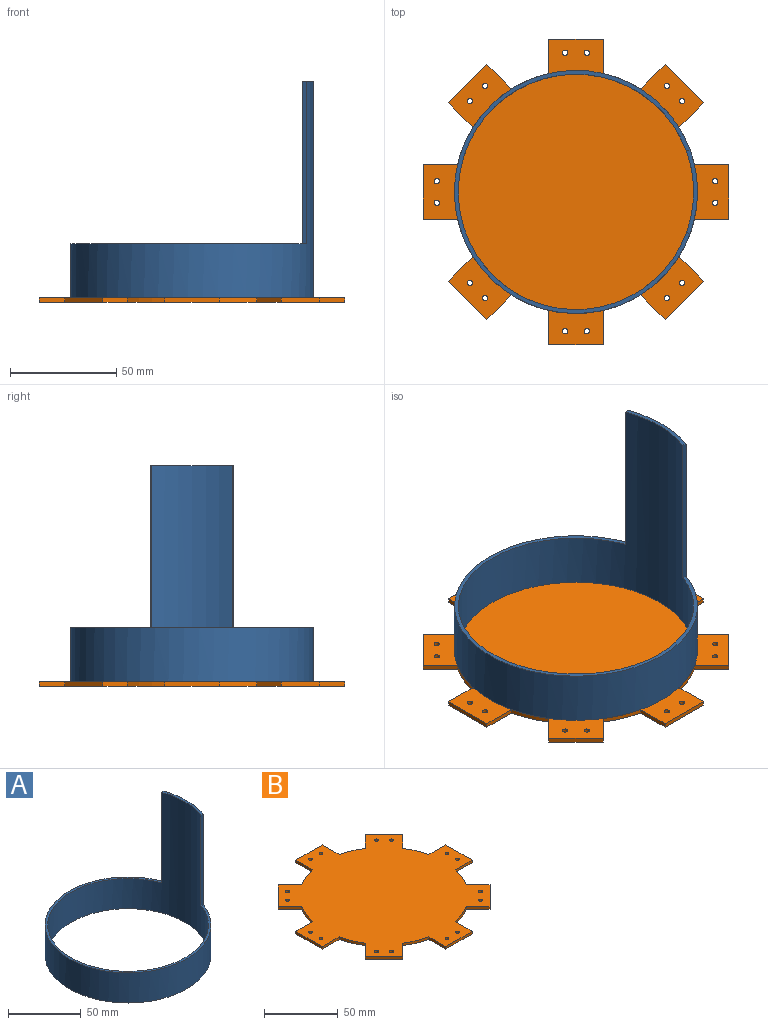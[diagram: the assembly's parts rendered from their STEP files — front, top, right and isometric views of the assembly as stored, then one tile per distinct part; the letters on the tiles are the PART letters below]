
ASSEMBLY  parts=2 mates=1
PART A: 7 faces, bbox 114.3x114.3x101.6 mm
  f0: plane 114.3x110.8mm, normal (0,0,1), area 573.9mm2, adj f1,f2,f4,f5
  f1: cylinder r=55.32mm len=110.64mm, axis (0,0,-1), area 11792.8mm2, adj f0,f3,f4,f5,f6
  f2: cylinder r=57.15mm len=114.3mm, axis (0,0,-1), area 12182.6mm2, adj f0,f3,f4,f5,f6
  f3: plane 114.3x114.3mm, normal (0,0,-1), area 646.2mm2, adj f1,f2
  f4: plane 76.2x1.72mm, normal (-0.34,0.94,0), area 139.4mm2, adj f0,f1,f2,f6
  f5: plane 76.2x1.72mm, normal (-0.34,-0.94,0), area 139.4mm2, adj f0,f1,f2,f6
  f6: plane 39.36x5.21mm, normal (0,0,1), area 72.3mm2, adj f1,f2,f4,f5
PART B: 50 faces, bbox 143.8x143.8x2 mm
  f0: cylinder r=57.15mm len=17.72mm, axis (0,0,-1), area 39.2mm2, adj f1,f31,f32,f33
  f1: plane 11.45x11.45mm, normal (-0.71,-0.71,0), area 32.9mm2, adj f0,f2,f32,f33
  f2: plane 17.96x17.96mm, normal (0.71,-0.71,0), area 51.6mm2, adj f1,f3,f32,f33
  f3: plane 11.45x11.45mm, normal (0.71,0.71,0), area 32.9mm2, adj f2,f4,f32,f33
  f4: cylinder r=57.15mm len=17.72mm, axis (0,0,-1), area 39.2mm2, adj f3,f5,f32,f33
  f5: plane 16.19x2.03mm, normal (0,-1,0), area 32.9mm2, adj f4,f6,f32,f33
  f6: plane 25.4x2.03mm, normal (1,0,0), area 51.6mm2, adj f5,f7,f32,f33
  f7: plane 16.19x2.03mm, normal (0,1,0), area 32.9mm2, adj f6,f8,f32,f33
  f8: cylinder r=57.15mm len=17.72mm, axis (0,0,-1), area 39.2mm2, adj f7,f9,f32,f33
  f9: plane 11.45x11.45mm, normal (0.71,-0.71,0), area 32.9mm2, adj f8,f10,f32,f33
  f10: plane 17.96x17.96mm, normal (0.71,0.71,0), area 51.6mm2, adj f9,f11,f32,f33
  f11: plane 11.45x11.45mm, normal (-0.71,0.71,0), area 32.9mm2, adj f10,f12,f32,f33
  f12: cylinder r=57.15mm len=17.72mm, axis (0,0,-1), area 39.2mm2, adj f11,f13,f32,f33
  f13: plane 16.19x2.03mm, normal (1,0,0), area 32.9mm2, adj f12,f14,f32,f33
  f14: plane 25.4x2.03mm, normal (0,1,0), area 51.6mm2, adj f13,f15,f32,f33
  f15: plane 16.19x2.03mm, normal (-1,0,0), area 32.9mm2, adj f14,f16,f32,f33
  f16: cylinder r=57.15mm len=17.72mm, axis (0,0,-1), area 39.2mm2, adj f15,f17,f32,f33
  f17: plane 11.45x11.45mm, normal (0.71,0.71,0), area 32.9mm2, adj f16,f18,f32,f33
  f18: plane 17.96x17.96mm, normal (-0.71,0.71,0), area 51.6mm2, adj f17,f19,f32,f33
  f19: plane 11.45x11.45mm, normal (-0.71,-0.71,0), area 32.9mm2, adj f18,f20,f32,f33
  f20: cylinder r=57.15mm len=17.72mm, axis (0,0,-1), area 39.2mm2, adj f19,f21,f32,f33
  f21: plane 16.19x2.03mm, normal (0,1,0), area 32.9mm2, adj f20,f22,f32,f33
  f22: plane 25.4x2.03mm, normal (-1,0,0), area 51.6mm2, adj f21,f23,f32,f33
  f23: plane 16.19x2.03mm, normal (0,-1,0), area 32.9mm2, adj f22,f24,f32,f33
  f24: cylinder r=57.15mm len=17.72mm, axis (0,0,-1), area 39.2mm2, adj f23,f25,f32,f33
  f25: plane 11.45x11.45mm, normal (-0.71,0.71,0), area 32.9mm2, adj f24,f26,f32,f33
  f26: plane 17.96x17.96mm, normal (-0.71,-0.71,0), area 51.6mm2, adj f25,f27,f32,f33
  f27: plane 11.45x11.45mm, normal (0.71,-0.71,0), area 32.9mm2, adj f26,f28,f32,f33
  f28: cylinder r=57.15mm len=17.72mm, axis (0,0,-1), area 39.2mm2, adj f27,f29,f32,f33
  f29: plane 16.19x2.03mm, normal (-1,0,0), area 32.9mm2, adj f28,f30,f32,f33
  f30: plane 25.4x2.03mm, normal (0,-1,0), area 51.6mm2, adj f29,f31,f32,f33
  f31: plane 16.19x2.03mm, normal (1,0,0), area 32.9mm2, adj f0,f30,f32,f33
  f32: plane 143.82x143.82mm, normal (0,0,1), area 13275.7mm2, adj f0,f1,f2,f3,f4,f5,f6,f7
  f33: plane 143.82x143.82mm, normal (0,0,-1), area 13275.7mm2, adj f0,f1,f2,f3,f4,f5,f6,f7
  f34: cylinder r=1.27mm len=2.54mm, axis (0,0,-1), area 16.2mm2, adj f32,f33
  f35: cylinder r=1.27mm len=2.54mm, axis (0,0,-1), area 16.2mm2, adj f32,f33
  f36: cylinder r=1.27mm len=2.54mm, axis (0,0,-1), area 16.2mm2, adj f32,f33
  f37: cylinder r=1.27mm len=2.54mm, axis (0,0,-1), area 16.2mm2, adj f32,f33
  f38: cylinder r=1.27mm len=2.54mm, axis (0,0,-1), area 16.2mm2, adj f32,f33
  f39: cylinder r=1.27mm len=2.54mm, axis (0,0,-1), area 16.2mm2, adj f32,f33
  f40: cylinder r=1.27mm len=2.54mm, axis (0,0,-1), area 16.2mm2, adj f32,f33
  f41: cylinder r=1.27mm len=2.54mm, axis (0,0,-1), area 16.2mm2, adj f32,f33
  f42: cylinder r=1.27mm len=2.54mm, axis (0,0,-1), area 16.2mm2, adj f32,f33
  f43: cylinder r=1.27mm len=2.54mm, axis (0,0,-1), area 16.2mm2, adj f32,f33
  f44: cylinder r=1.27mm len=2.54mm, axis (0,0,-1), area 16.2mm2, adj f32,f33
  f45: cylinder r=1.27mm len=2.54mm, axis (0,0,-1), area 16.2mm2, adj f32,f33
  f46: cylinder r=1.27mm len=2.54mm, axis (0,0,-1), area 16.2mm2, adj f32,f33
  f47: cylinder r=1.27mm len=2.54mm, axis (0,0,-1), area 16.2mm2, adj f32,f33
  f48: cylinder r=1.27mm len=2.54mm, axis (0,0,-1), area 16.2mm2, adj f32,f33
  f49: cylinder r=1.27mm len=2.54mm, axis (0,0,-1), area 16.2mm2, adj f32,f33
PLACE A t=(0,0,2.03)mm
PLACE B at identity
MATE planar A.f1 <-> B.f28  axis (0,0,-1) through (0,0,2.03)mm
